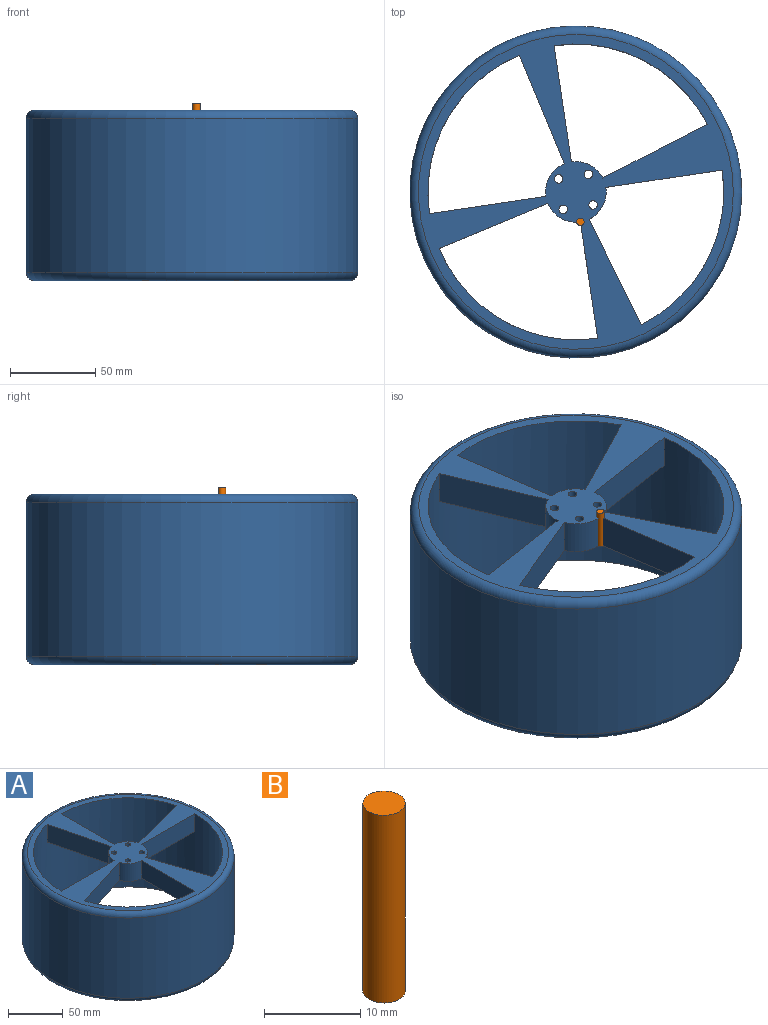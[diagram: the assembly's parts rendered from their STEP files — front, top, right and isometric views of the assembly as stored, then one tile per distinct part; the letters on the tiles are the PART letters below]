
ASSEMBLY  parts=2 mates=1
PART A: 23 faces, bbox 210.6x210.6x100 mm
  f0: cylinder r=86.75mm len=173.49mm, axis (0,0,-1), area 52557.8mm2, adj f2,f3,f4,f6,f7,f9,f10,f12
  f1: cylinder r=97.3mm len=194.6mm, axis (0,0,-1), area 55021mm2, adj f21,f22
  f2: plane 184.6x184.6mm, normal (0,0,1), area 8079.6mm2, adj f0,f4,f5,f6,f7,f8,f9,f10
  f3: plane 184.6x184.6mm, normal (0,0,-1), area 3123.7mm2, adj f0,f21
  f4: plane 65.32x22.17mm, normal (0.95,0.32,0), area 1379.5mm2, adj f0,f2,f5,f16
  f5: cylinder r=17.77mm len=20mm, axis (0,0,1), area 441.9mm2, adj f2,f4,f6,f16
  f6: plane 68.98x20mm, normal (0,-1,0), area 1379.5mm2, adj f0,f2,f5,f16
  f7: plane 66.95x20mm, normal (-0.24,0.97,0), area 1379.5mm2, adj f0,f2,f8,f16
  f8: cylinder r=17.77mm len=20mm, axis (0,0,1), area 471.8mm2, adj f2,f7,f9,f16
  f9: plane 68.98x20mm, normal (1,0,0), area 1379.5mm2, adj f0,f2,f8,f16
  f10: plane 66.94x20mm, normal (-0.97,-0.24,0), area 1379.5mm2, adj f0,f2,f11,f16
  f11: cylinder r=17.77mm len=20mm, axis (0,0,1), area 471.7mm2, adj f2,f10,f12,f16
  f12: plane 68.98x20mm, normal (0,1,0), area 1379.5mm2, adj f0,f2,f11,f16
  f13: plane 65.74x20.89mm, normal (0.3,-0.95,0), area 1379.5mm2, adj f0,f2,f14,f16
  f14: cylinder r=17.77mm len=20mm, axis (0,0,1), area 448.9mm2, adj f2,f13,f15,f16
  f15: plane 68.98x20mm, normal (-1,0,0), area 1379.5mm2, adj f0,f2,f14,f16
  f16: plane 173.49x173.49mm, normal (0,0,-1), area 4955.8mm2, adj f0,f4,f5,f6,f7,f8,f9,f10
  f17: cylinder r=2.5mm len=20mm, axis (0,0,1), area 314.2mm2, adj f2,f16
  f18: cylinder r=2.5mm len=20mm, axis (0,0,1), area 314.2mm2, adj f2,f16
  f19: cylinder r=2.5mm len=20mm, axis (0,0,1), area 314.2mm2, adj f2,f16
  f20: cylinder r=2.5mm len=20mm, axis (0,0,1), area 314.2mm2, adj f2,f16
  f21: torus R=92.3mm, axis (0,0,1), area 4711.8mm2, adj f1,f3
  f22: torus R=92.3mm, axis (0,0,1), area 4711.8mm2, adj f1,f2
PART B: 3 faces, bbox 4.4x4.4x23.9 mm
  f0: cylinder r=2.2mm len=23.93mm, axis (0,0,-1), area 330.8mm2, adj f1,f2
  f1: plane 4.4x4.4mm, normal (0,0,1), area 15.2mm2, adj f0
  f2: plane 4.4x4.4mm, normal (0,0,-1), area 15.2mm2, adj f0
PLACE A rot(axis=(0,0,1),98.5deg) t=(-10.23,13.33,0)mm
PLACE B rot(axis=(0,0,1),8.5deg) t=(-7.61,-4.24,80)mm
MATE fastened B.f0 <-> A.f16  axis (0,0,-1) through (-7.61,-4.24,80)mm
